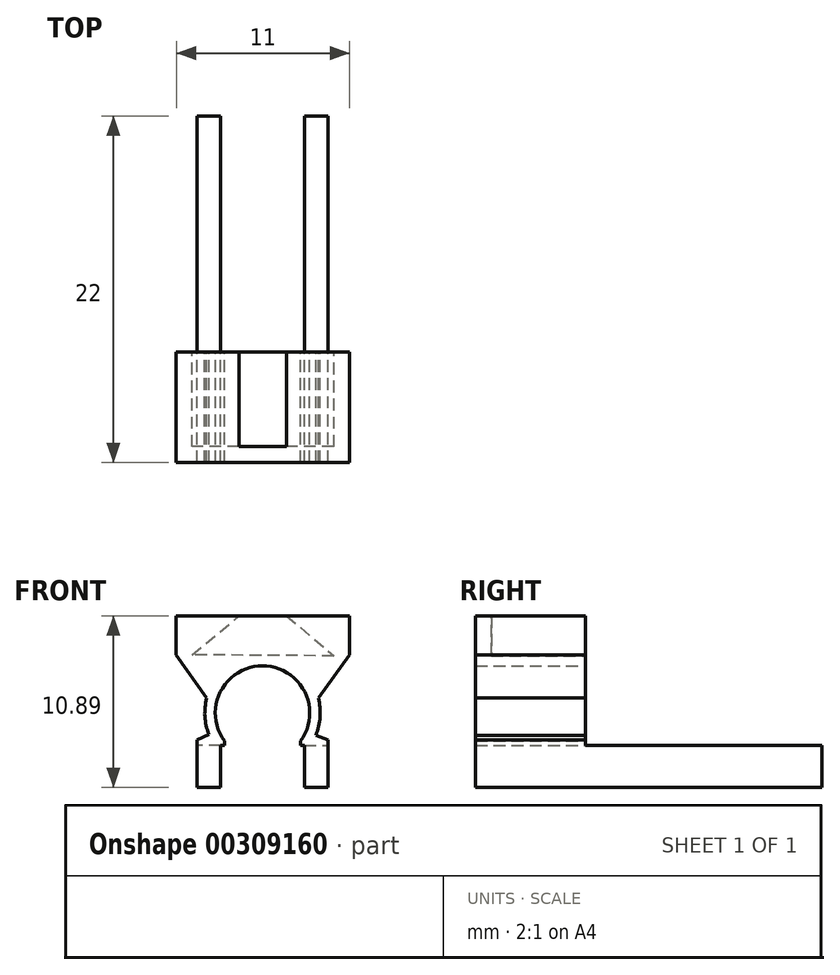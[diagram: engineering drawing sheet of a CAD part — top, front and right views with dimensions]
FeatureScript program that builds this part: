
annotation { "Feature Type Name" : "Feature", "Feature Type Description" : "" }
export const myFeature = defineFeature(function(context is Context, id is Id, definition is map)
    precondition{}
    {
        {
            var Q0;
            Q0=qCreatedBy(makeId("Front.planeOp"),FACE);
            var sketch = newSketch(context, id + "F0", { "sketchPlane" : qUnion([Q0])});
            skLineSegment(sketch, "E0", {"start": v(-3.34, -1.58) * mm, "end": v(-3.32, -1.6) * mm});
            skArc(sketch, "E1.trimOffspring", {"start": v(3.45, -1.63) * mm, "mid": v(0.1, 3.44) * mm, "end": v(-3.34, -1.58) * mm});
            skLineSegment(sketch, "E2", {"start": v(-3.32, -1.6) * mm, "end": v(-3.32, -2.28) * mm});
            skLineSegment(sketch, "E3", {"start": v(-3.32, -4.95) * mm, "end": v(-2.59, -4.95) * mm});
            skLineSegment(sketch, "E4", {"start": v(3.45, -1.63) * mm, "end": v(3.45, -2.28) * mm});
            skLineSegment(sketch, "E5", {"start": v(3.45, -4.95) * mm, "end": v(2.72, -4.95) * mm});
            skLineSegment(sketch, "E6", {"start": v(-4.09, -1.94) * mm, "end": v(-4.09, -4.95) * mm});
            skLineSegment(sketch, "E7", {"start": v(-4.09, -4.95) * mm, "end": v(-3.32, -4.95) * mm});
            skLineSegment(sketch, "E8.MirrorCS", {"start": v(4.22, -1.94) * mm, "end": v(4.22, -4.95) * mm});
            skLineSegment(sketch, "E9.MirrorCS", {"start": v(4.22, -4.95) * mm, "end": v(3.45, -4.95) * mm});
            skLineSegment(sketch, "E10", {"start": v(-4.09, -1.94) * mm, "end": v(-3.32, -1.6) * mm});
            skLineSegment(sketch, "E11", {"start": v(4.22, -1.94) * mm, "end": v(3.45, -1.63) * mm});
            skLineSegment(sketch, "E12", {"start": v(0.1, 3.44) * mm, "end": v(-4.4, 3.47) * mm});
            skLineSegment(sketch, "E13", {"start": v(0.1, 3.44) * mm, "end": v(4.6, 3.4) * mm});
            skLineSegment(sketch, "E14", {"start": v(0.1, 3.44) * mm, "end": v(0.1, 5.94) * mm, "construction": true});
            skLineSegment(sketch, "E15", {"start": v(-4.4, 3.47) * mm, "end": v(-1.41, 5.94) * mm});
            skLineSegment(sketch, "E16", {"start": v(1.6, 5.94) * mm, "end": v(4.6, 3.4) * mm});
            skLineSegment(sketch, "E17", {"start": v(-1.41, 5.94) * mm, "end": v(-5.41, 5.94) * mm});
            skLineSegment(sketch, "E18", {"start": v(-5.41, 5.94) * mm, "end": v(-5.41, 3.47) * mm});
            skLineSegment(sketch, "E19", {"start": v(-5.41, 3.47) * mm, "end": v(-3.48, 0.72) * mm});
            skLineSegment(sketch, "E20", {"start": v(1.6, 5.94) * mm, "end": v(5.59, 5.94) * mm});
            skLineSegment(sketch, "E21", {"start": v(5.59, 5.94) * mm, "end": v(5.59, 3.47) * mm});
            skLineSegment(sketch, "E22", {"start": v(5.59, 3.47) * mm, "end": v(3.6, 0.72) * mm});
            skLineSegment(sketch, "E23", {"start": v(-1.41, 5.94) * mm, "end": v(1.6, 5.94) * mm});
            skLineSegment(sketch, "E24", {"start": v(-3.32, -2.28) * mm, "end": v(-4.09, -2.28) * mm});
            skLineSegment(sketch, "E25", {"start": v(3.45, -2.28) * mm, "end": v(4.22, -2.28) * mm});
            skLineSegment(sketch, "E26", {"start": v(3.45, -2.28) * mm, "end": v(3.45, -4.95) * mm, "construction": true});
            skLineSegment(sketch, "E27.0", {"start": v(2.72, -2.28) * mm, "end": v(2.72, -4.95) * mm});
            skLineSegment(sketch, "E28.0", {"start": v(-2.59, -2.28) * mm, "end": v(-2.59, -4.95) * mm});
            skLineSegment(sketch, "E29", {"start": v(-2.59, -2.28) * mm, "end": v(-3.32, -2.28) * mm});
            skLineSegment(sketch, "E30", {"start": v(2.72, -2.28) * mm, "end": v(3.45, -2.28) * mm});
            skArc(sketch, "E31", {"start": v(2.48, -2) * mm, "mid": v(0.06, 2.77) * mm, "end": v(-2.36, -2) * mm});
            skLineSegment(sketch, "E32", {"start": v(2.72, -2.28) * mm, "end": v(2.48, -2.28) * mm});
            skLineSegment(sketch, "E33", {"start": v(-2.59, -2.28) * mm, "end": v(-2.36, -2.28) * mm});
            skLineSegment(sketch, "E34", {"start": v(-2.36, -2.28) * mm, "end": v(-2.36, -2) * mm});
            skLineSegment(sketch, "E35", {"start": v(2.48, -2.28) * mm, "end": v(2.48, -2) * mm});
            skPoint(sketch, "E36.orphan", {"position": v(2.25, -2.28) * mm});
            skPoint(sketch, "E37.orphan", {"position": v(-2.12, -2.28) * mm});
            skSolve(sketch);
        }
        {
            var Q0;
            Q0=qSketchRegion(id+"F0",true);
            extrude(context, id + "F1", {"entities" : qUnion([Q0]), "depth" : 7 * mm});
        }
        {
            var Q0;
            Q0=makeQuery(id+"F0.imprint","IMPRINT",FACE,{"disambiguationData":[TD([[makeQuery(id+"F0.imprint","IMPRINT",EDGE,{"derivedFrom":sQuery(id+"F0.wireOp",EDGE,"E12")}),-1.0]])]});
            extrude(context, id + "F2", {"entities" : qUnion([Q0]), "operationType" : NewBodyOperationType.REMOVE, "depth" : 6 * mm, "offsetDistance" : 25 * mm});
        }
        {
            var Q0;
            Q0=makeQuery(id+"F0.imprint","IMPRINT",FACE,{"disambiguationData":[TD([[makeQuery(id+"F0.imprint","IMPRINT",EDGE,{"derivedFrom":sQuery(id+"F0.wireOp",EDGE,"E5")}),-1.0]])]});
            var Q1;
            Q1=makeQuery(id+"F0.imprint","IMPRINT",FACE,{"disambiguationData":[TD([[makeQuery(id+"F0.imprint","IMPRINT",EDGE,{"derivedFrom":sQuery(id+"F0.wireOp",EDGE,"E3")}),1.0]])]});
            extrude(context, id + "F3", {"entities" : qUnion([Q0, Q1]), "operationType" : NewBodyOperationType.ADD, "oppositeDirection" : true, "depth" : 15 * mm, "offsetDistance" : 25 * mm});
        }
    });
